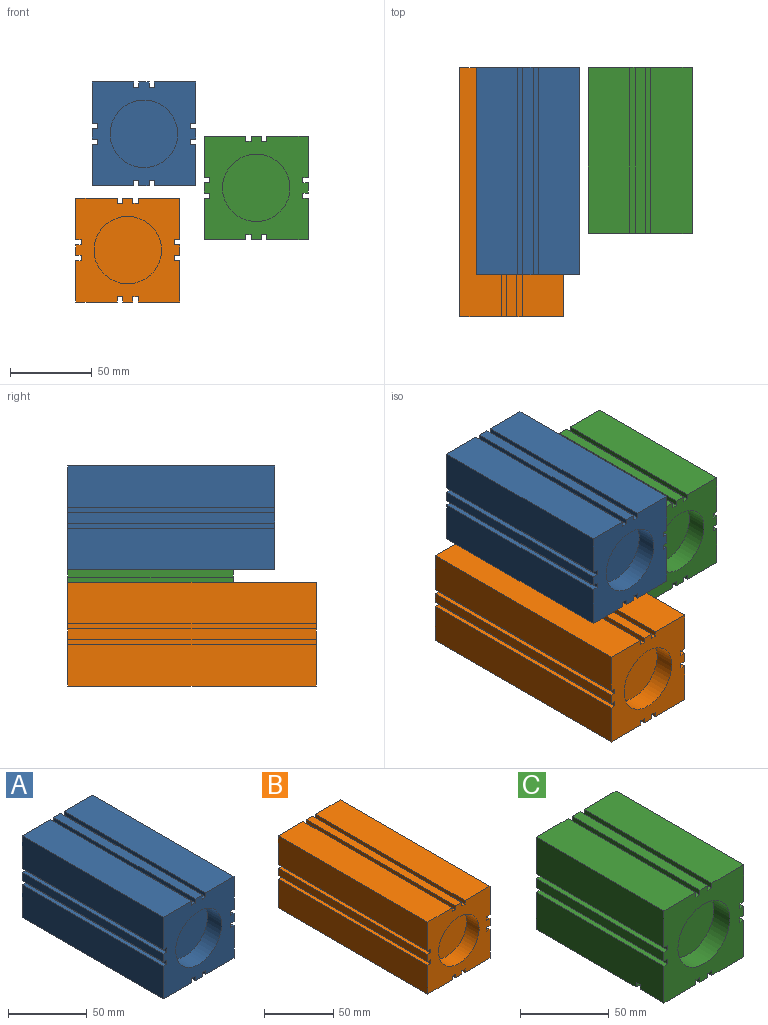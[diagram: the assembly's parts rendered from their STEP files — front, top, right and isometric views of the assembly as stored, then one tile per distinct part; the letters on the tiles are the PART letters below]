
ASSEMBLY  parts=3 mates=2
PART A: 40 faces, bbox 63.5x127x63.5 mm
  f0: plane 127x25.4mm, normal (0,0,-1), area 3225.8mm2, adj f2,f4,f13,f37
  f1: plane 127x6.35mm, normal (0,0,-1), area 806.4mm2, adj f2,f13,f34,f38
  f2: plane 63.5x63.5mm, normal (0,-1,0), area 2613.6mm2, adj f0,f1,f3,f4,f5,f6,f7,f8
  f3: plane 127x6.35mm, normal (-1,0,0), area 806.4mm2, adj f2,f13,f28,f32
  f4: plane 127x25.4mm, normal (-1,0,0), area 3225.8mm2, adj f0,f2,f13,f29
  f5: plane 127x25.4mm, normal (0,0,1), area 3225.8mm2, adj f2,f9,f13,f26
  f6: plane 127x6.35mm, normal (0,0,1), area 806.4mm2, adj f2,f13,f23,f25
  f7: plane 127x25.4mm, normal (1,0,0), area 3225.8mm2, adj f2,f10,f13,f19
  f8: plane 127x6.35mm, normal (1,0,0), area 806.4mm2, adj f2,f13,f17,f20
  f9: plane 127x25.4mm, normal (-1,0,0), area 3225.8mm2, adj f2,f5,f13,f31
  f10: plane 127x25.4mm, normal (0,0,-1), area 3225.8mm2, adj f2,f7,f13,f35
  f11: plane 127x25.4mm, normal (1,0,0), area 3225.8mm2, adj f2,f12,f13,f16
  f12: plane 127x25.4mm, normal (0,0,1), area 3225.8mm2, adj f2,f11,f13,f22
  f13: plane 63.5x63.5mm, normal (0,1,0), area 3951.6mm2, adj f0,f1,f3,f4,f5,f6,f7,f8
  f14: cylinder r=20.64mm len=41.28mm, axis (0,-1,0), area 1646.8mm2, adj f2,f15
  f15: plane 41.28x41.28mm, normal (0,-1,0), area 1338mm2, adj f14
  f16: plane 127x3.18mm, normal (0,0,-1), area 403.2mm2, adj f2,f11,f13,f18
  f17: plane 127x3.18mm, normal (0,0,1), area 403.2mm2, adj f2,f8,f13,f18
  f18: plane 127x3.18mm, normal (1,0,0), area 403.2mm2, adj f2,f13,f16,f17
  f19: plane 127x3.18mm, normal (0,0,1), area 403.2mm2, adj f2,f7,f13,f21
  f20: plane 127x3.18mm, normal (0,0,-1), area 403.2mm2, adj f2,f8,f13,f21
  f21: plane 127x3.18mm, normal (1,0,0), area 403.2mm2, adj f2,f13,f19,f20
  f22: plane 127x3.18mm, normal (-1,0,0), area 403.2mm2, adj f2,f12,f13,f24
  f23: plane 127x3.18mm, normal (1,0,0), area 403.2mm2, adj f2,f6,f13,f24
  f24: plane 127x3.18mm, normal (0,0,1), area 403.2mm2, adj f2,f13,f22,f23
  f25: plane 127x3.18mm, normal (-1,0,0), area 403.2mm2, adj f2,f6,f13,f27
  f26: plane 127x3.18mm, normal (1,0,0), area 403.2mm2, adj f2,f5,f13,f27
  f27: plane 127x3.18mm, normal (0,0,1), area 403.2mm2, adj f2,f13,f25,f26
  f28: plane 127x3.18mm, normal (0,0,-1), area 403.2mm2, adj f2,f3,f13,f30
  f29: plane 127x3.18mm, normal (0,0,1), area 403.2mm2, adj f2,f4,f13,f30
  f30: plane 127x3.18mm, normal (-1,0,0), area 403.2mm2, adj f2,f13,f28,f29
  f31: plane 127x3.18mm, normal (0,0,-1), area 403.2mm2, adj f2,f9,f13,f33
  f32: plane 127x3.18mm, normal (0,0,1), area 403.2mm2, adj f2,f3,f13,f33
  f33: plane 127x3.18mm, normal (-1,0,0), area 403.2mm2, adj f2,f13,f31,f32
  f34: plane 127x3.18mm, normal (1,0,0), area 403.2mm2, adj f1,f2,f13,f36
  f35: plane 127x3.18mm, normal (-1,0,0), area 403.2mm2, adj f2,f10,f13,f36
  f36: plane 127x3.18mm, normal (0,0,-1), area 403.2mm2, adj f2,f13,f34,f35
  f37: plane 127x3.18mm, normal (1,0,0), area 403.2mm2, adj f0,f2,f13,f39
  f38: plane 127x3.18mm, normal (-1,0,0), area 403.2mm2, adj f1,f2,f13,f39
  f39: plane 127x3.18mm, normal (0,0,-1), area 403.2mm2, adj f2,f13,f37,f38
PART B: 40 faces, bbox 63.5x152.4x63.5 mm
  f0: plane 152.4x25.4mm, normal (0,0,-1), area 3871mm2, adj f2,f4,f13,f37
  f1: plane 152.4x6.35mm, normal (0,0,-1), area 967.7mm2, adj f2,f13,f34,f38
  f2: plane 63.5x63.5mm, normal (0,-1,0), area 2613.6mm2, adj f0,f1,f3,f4,f5,f6,f7,f8
  f3: plane 152.4x6.35mm, normal (-1,0,0), area 967.7mm2, adj f2,f13,f28,f32
  f4: plane 152.4x25.4mm, normal (-1,0,0), area 3871mm2, adj f0,f2,f13,f29
  f5: plane 152.4x25.4mm, normal (0,0,1), area 3871mm2, adj f2,f9,f13,f26
  f6: plane 152.4x6.35mm, normal (0,0,1), area 967.7mm2, adj f2,f13,f23,f25
  f7: plane 152.4x25.4mm, normal (1,0,0), area 3871mm2, adj f2,f10,f13,f19
  f8: plane 152.4x6.35mm, normal (1,0,0), area 967.7mm2, adj f2,f13,f17,f20
  f9: plane 152.4x25.4mm, normal (-1,0,0), area 3871mm2, adj f2,f5,f13,f31
  f10: plane 152.4x25.4mm, normal (0,0,-1), area 3871mm2, adj f2,f7,f13,f35
  f11: plane 152.4x25.4mm, normal (1,0,0), area 3871mm2, adj f2,f12,f13,f16
  f12: plane 152.4x25.4mm, normal (0,0,1), area 3871mm2, adj f2,f11,f13,f22
  f13: plane 63.5x63.5mm, normal (0,1,0), area 3951.6mm2, adj f0,f1,f3,f4,f5,f6,f7,f8
  f14: cylinder r=20.64mm len=41.28mm, axis (0,-1,0), area 1646.8mm2, adj f2,f15
  f15: plane 41.28x41.28mm, normal (0,-1,0), area 1338mm2, adj f14
  f16: plane 152.4x3.18mm, normal (0,0,-1), area 483.9mm2, adj f2,f11,f13,f18
  f17: plane 152.4x3.18mm, normal (0,0,1), area 483.9mm2, adj f2,f8,f13,f18
  f18: plane 152.4x3.18mm, normal (1,0,0), area 483.9mm2, adj f2,f13,f16,f17
  f19: plane 152.4x3.18mm, normal (0,0,1), area 483.9mm2, adj f2,f7,f13,f21
  f20: plane 152.4x3.18mm, normal (0,0,-1), area 483.9mm2, adj f2,f8,f13,f21
  f21: plane 152.4x3.18mm, normal (1,0,0), area 483.9mm2, adj f2,f13,f19,f20
  f22: plane 152.4x3.18mm, normal (-1,0,0), area 483.9mm2, adj f2,f12,f13,f24
  f23: plane 152.4x3.18mm, normal (1,0,0), area 483.9mm2, adj f2,f6,f13,f24
  f24: plane 152.4x3.18mm, normal (0,0,1), area 483.9mm2, adj f2,f13,f22,f23
  f25: plane 152.4x3.18mm, normal (-1,0,0), area 483.9mm2, adj f2,f6,f13,f27
  f26: plane 152.4x3.18mm, normal (1,0,0), area 483.9mm2, adj f2,f5,f13,f27
  f27: plane 152.4x3.18mm, normal (0,0,1), area 483.9mm2, adj f2,f13,f25,f26
  f28: plane 152.4x3.18mm, normal (0,0,-1), area 483.9mm2, adj f2,f3,f13,f30
  f29: plane 152.4x3.18mm, normal (0,0,1), area 483.9mm2, adj f2,f4,f13,f30
  f30: plane 152.4x3.18mm, normal (-1,0,0), area 483.9mm2, adj f2,f13,f28,f29
  f31: plane 152.4x3.18mm, normal (0,0,-1), area 483.9mm2, adj f2,f9,f13,f33
  f32: plane 152.4x3.18mm, normal (0,0,1), area 483.9mm2, adj f2,f3,f13,f33
  f33: plane 152.4x3.18mm, normal (-1,0,0), area 483.9mm2, adj f2,f13,f31,f32
  f34: plane 152.4x3.18mm, normal (1,0,0), area 483.9mm2, adj f1,f2,f13,f36
  f35: plane 152.4x3.18mm, normal (-1,0,0), area 483.9mm2, adj f2,f10,f13,f36
  f36: plane 152.4x3.18mm, normal (0,0,-1), area 483.9mm2, adj f2,f13,f34,f35
  f37: plane 152.4x3.18mm, normal (1,0,0), area 483.9mm2, adj f0,f2,f13,f39
  f38: plane 152.4x3.18mm, normal (-1,0,0), area 483.9mm2, adj f1,f2,f13,f39
  f39: plane 152.4x3.18mm, normal (0,0,-1), area 483.9mm2, adj f2,f13,f37,f38
PART C: 52 faces, bbox 63.5x101.6x63.5 mm
  f0: plane 79.38x25.4mm, normal (0,0,-1), area 2016.1mm2, adj f3,f20,f43,f48
  f1: plane 79.38x6.35mm, normal (0,0,-1), area 504mm2, adj f20,f41,f44,f46
  f2: plane 79.38x25.4mm, normal (0,0,-1), area 2016.1mm2, adj f14,f20,f42,f51
  f3: plane 101.6x25.4mm, normal (-1,0,0), area 2570.6mm2, adj f0,f8,f10,f20,f36,f45,f48,f49
  f4: plane 19.05x3.18mm, normal (1,0,0), area 60.5mm2, adj f9,f10,f45,f47
  f5: plane 19.05x3.18mm, normal (-1,0,0), area 60.5mm2, adj f10,f17,f45,f50
  f6: plane 19.05x3.18mm, normal (1,0,0), area 60.5mm2, adj f8,f10,f45,f49
  f7: plane 19.05x3.18mm, normal (-1,0,0), area 60.5mm2, adj f9,f10,f45,f47
  f8: plane 25.4x19.05mm, normal (0,0,-1), area 483.9mm2, adj f3,f6,f10,f49
  f9: plane 19.05x6.35mm, normal (0,0,-1), area 121mm2, adj f4,f7,f10,f47
  f10: plane 63.5x63.5mm, normal (0,-1,0), area 2613.6mm2, adj f3,f4,f5,f6,f7,f8,f9,f11
  f11: plane 101.6x6.35mm, normal (-1,0,0), area 645.2mm2, adj f10,f20,f35,f39
  f12: plane 101.6x25.4mm, normal (0,0,1), area 2580.6mm2, adj f10,f16,f20,f33
  f13: plane 101.6x6.35mm, normal (0,0,1), area 645.2mm2, adj f10,f20,f30,f32
  f14: plane 101.6x25.4mm, normal (1,0,0), area 2570.6mm2, adj f2,f10,f17,f20,f26,f45,f50,f51
  f15: plane 101.6x6.35mm, normal (1,0,0), area 645.2mm2, adj f10,f20,f24,f27
  f16: plane 101.6x25.4mm, normal (-1,0,0), area 2580.6mm2, adj f10,f12,f20,f38
  f17: plane 25.4x19.05mm, normal (0,0,-1), area 483.9mm2, adj f5,f10,f14,f50
  f18: plane 101.6x25.4mm, normal (1,0,0), area 2580.6mm2, adj f10,f19,f20,f23
  f19: plane 101.6x25.4mm, normal (0,0,1), area 2580.6mm2, adj f10,f18,f20,f29
  f20: plane 63.5x63.5mm, normal (0,1,0), area 3951.6mm2, adj f0,f1,f2,f3,f11,f12,f13,f14
  f21: cylinder r=20.64mm len=41.28mm, axis (0,-1,0), area 1646.8mm2, adj f10,f22
  f22: plane 41.28x41.28mm, normal (0,-1,0), area 1338mm2, adj f21
  f23: plane 101.6x3.18mm, normal (0,0,-1), area 322.6mm2, adj f10,f18,f20,f25
  f24: plane 101.6x3.18mm, normal (0,0,1), area 322.6mm2, adj f10,f15,f20,f25
  f25: plane 101.6x3.18mm, normal (1,0,0), area 322.6mm2, adj f10,f20,f23,f24
  f26: plane 101.6x3.18mm, normal (0,0,1), area 322.6mm2, adj f10,f14,f20,f28
  f27: plane 101.6x3.18mm, normal (0,0,-1), area 322.6mm2, adj f10,f15,f20,f28
  f28: plane 101.6x3.18mm, normal (1,0,0), area 322.6mm2, adj f10,f20,f26,f27
  f29: plane 101.6x3.18mm, normal (-1,0,0), area 322.6mm2, adj f10,f19,f20,f31
  f30: plane 101.6x3.18mm, normal (1,0,0), area 322.6mm2, adj f10,f13,f20,f31
  f31: plane 101.6x3.18mm, normal (0,0,1), area 322.6mm2, adj f10,f20,f29,f30
  f32: plane 101.6x3.18mm, normal (-1,0,0), area 322.6mm2, adj f10,f13,f20,f34
  f33: plane 101.6x3.18mm, normal (1,0,0), area 322.6mm2, adj f10,f12,f20,f34
  f34: plane 101.6x3.18mm, normal (0,0,1), area 322.6mm2, adj f10,f20,f32,f33
  f35: plane 101.6x3.18mm, normal (0,0,-1), area 322.6mm2, adj f10,f11,f20,f37
  f36: plane 101.6x3.18mm, normal (0,0,1), area 322.6mm2, adj f3,f10,f20,f37
  f37: plane 101.6x3.18mm, normal (-1,0,0), area 322.6mm2, adj f10,f20,f35,f36
  f38: plane 101.6x3.18mm, normal (0,0,-1), area 322.6mm2, adj f10,f16,f20,f40
  f39: plane 101.6x3.18mm, normal (0,0,1), area 322.6mm2, adj f10,f11,f20,f40
  f40: plane 101.6x3.18mm, normal (-1,0,0), area 322.6mm2, adj f10,f20,f38,f39
  f41: plane 79.38x3.18mm, normal (1,0,0), area 252mm2, adj f1,f20,f45,f46
  f42: plane 79.38x3.18mm, normal (-1,0,0), area 252mm2, adj f2,f20,f45,f51
  f43: plane 79.38x3.18mm, normal (1,0,0), area 252mm2, adj f0,f20,f45,f48
  f44: plane 79.38x3.18mm, normal (-1,0,0), area 252mm2, adj f1,f20,f45,f46
  f45: plane 101.6x63.5mm, normal (0,0,-1), area 826.6mm2, adj f3,f4,f5,f6,f7,f10,f14,f20
  f46: plane 6.35x3.18mm, normal (0,-1,0), area 20.2mm2, adj f1,f41,f44,f45
  f47: plane 6.35x3.18mm, normal (0,1,0), area 20.2mm2, adj f4,f7,f9,f45
  f48: plane 25.4x3.18mm, normal (0,-1,0), area 80.6mm2, adj f0,f3,f43,f45
  f49: plane 25.4x3.18mm, normal (0,1,0), area 80.6mm2, adj f3,f6,f8,f45
  f50: plane 25.4x3.18mm, normal (0,1,0), area 80.6mm2, adj f5,f14,f17,f45
  f51: plane 25.4x3.18mm, normal (0,-1,0), area 80.6mm2, adj f2,f14,f42,f45
PLACE A t=(89.37,66.97,1.36)mm
PLACE B t=(79.48,66.97,-69.81)mm
PLACE C t=(158.12,66.97,-31.7)mm
MATE planar B.f14 <-> A.f14  axis (0,1,0) through (111.23,66.97,-38.06)mm
MATE planar A.f13 <-> C.f21  axis (0,1,0) through (149.7,66.97,39.46)mm
